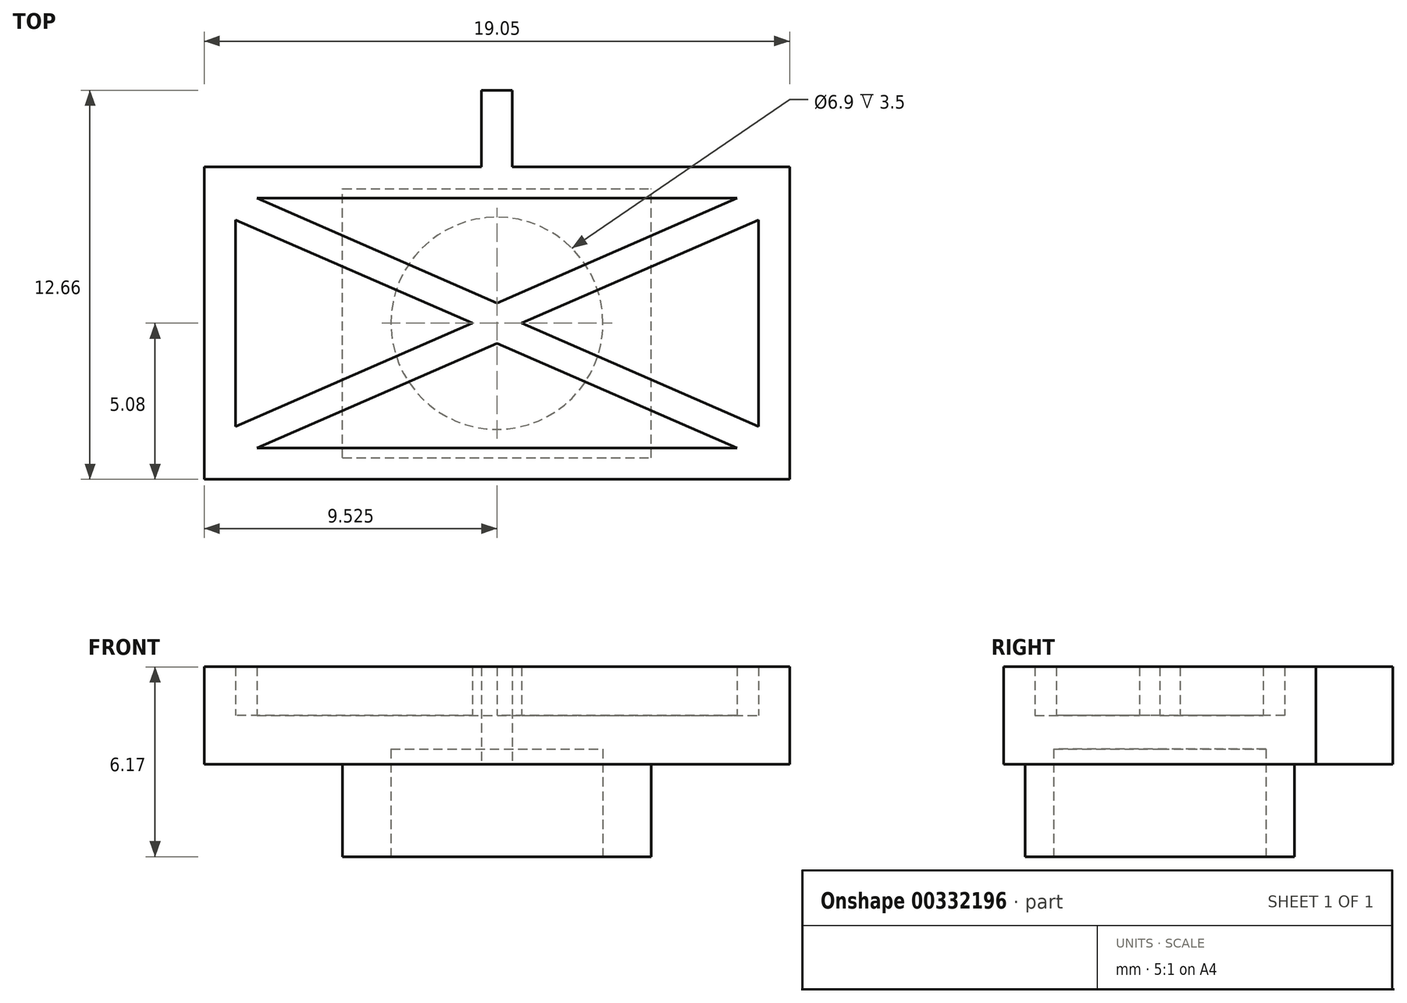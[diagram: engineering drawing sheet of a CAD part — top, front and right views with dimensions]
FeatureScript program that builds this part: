
annotation { "Feature Type Name" : "Feature", "Feature Type Description" : "" }
export const myFeature = defineFeature(function(context is Context, id is Id, definition is map)
    precondition{}
    {
        {
            var Q0;
            Q0=qCreatedBy(makeId("Top.planeOp"),FACE);
            var sketch = newSketch(context, id + "F0", { "sketchPlane" : qUnion([Q0])});
            skLineSegment(sketch, "E0.bottom", {"start": v(-19.05, 10.16) * mm, "end": v(0, 10.16) * mm});
            skLineSegment(sketch, "E0.top", {"start": v(-19.05, 0) * mm, "end": v(0, 0) * mm});
            skLineSegment(sketch, "E0.left", {"start": v(-19.05, 10.16) * mm, "end": v(-19.05, 0) * mm});
            skLineSegment(sketch, "E0.right", {"start": v(0, 10.16) * mm, "end": v(0, 0) * mm});
            skLineSegment(sketch, "E1", {"start": v(-9.52, 10.16) * mm, "end": v(-9.52, 0) * mm, "construction": true});
            skLineSegment(sketch, "E2.bottom", {"start": v(-10.02, 12.66) * mm, "end": v(-9.02, 12.66) * mm});
            skLineSegment(sketch, "E2.top", {"start": v(-10.02, 10.16) * mm, "end": v(-9.02, 10.16) * mm});
            skLineSegment(sketch, "E2.left", {"start": v(-10.02, 12.66) * mm, "end": v(-10.02, 10.16) * mm});
            skLineSegment(sketch, "E2.right", {"start": v(-9.02, 12.66) * mm, "end": v(-9.02, 10.16) * mm});
            skSolve(sketch);
        }
        {
            var Q0;
            Q0=qSketchRegion(id+"F0",true);
            extrude(context, id + "F1", {"entities" : qUnion([Q0]), "depth" : 3.17 * mm});
        }
        {
            var Q0;
            Q0=makeQuery(id+"F1.opExtrude","CAP_FACE",FACE,{"disambiguationData":[OSD([sQuery(id+"F0.wireOp",EDGE,"E0.bottom"),sQuery(id+"F0.wireOp",EDGE,"E0.top"),sQuery(id+"F0.wireOp",EDGE,"E0.left"),sQuery(id+"F0.wireOp",EDGE,"E0.right")])],"isStart":false});
            var sketch = newSketch(context, id + "F2", { "sketchPlane" : qUnion([Q0])});
            skLineSegment(sketch, "E3.bottom", {"start": v(-18.03, 9.14) * mm, "end": v(-1.02, 9.14) * mm});
            skLineSegment(sketch, "E3.top", {"start": v(-18.03, 1.02) * mm, "end": v(-1.02, 1.02) * mm});
            skLineSegment(sketch, "E3.left", {"start": v(-18.03, 9.14) * mm, "end": v(-18.03, 1.02) * mm});
            skLineSegment(sketch, "E3.right", {"start": v(-1.02, 9.14) * mm, "end": v(-1.02, 1.02) * mm});
            skSolve(sketch);
        }
        {
            var Q0;
            Q0=qSketchRegion(id+"F2",true);
            extrude(context, id + "F3", {"entities" : qUnion([Q0]), "operationType" : NewBodyOperationType.REMOVE, "oppositeDirection" : true, "depth" : 1.59 * mm});
        }
        {
            var Q0;
            {var subQ1=sQuery(id+"F2.wireOp",EDGE,"E3.top");var subQ4=makeQuery(id+"F3.boolean.opBoolean","COPY",FACE,{"derivedFrom":makeQuery(id+"F3.opExtrude","SWEPT_FACE",FACE,{"disambiguationData":[OSD([subQ1])]})});var subQ6=sQuery(id+"F2.wireOp",EDGE,"E3.right");Q0=makeQuery(id+"FbiU5rRMadnEj1Y_1.boolean.opBoolean","SPLIT",FACE,{"disambiguationData":[TD([subQ4])],"derivedFrom":makeQuery(id+"FD6hazfNaiJcgqe_1.boolean.opBoolean","SPLIT",FACE,{"disambiguationData":[TD([subQ4])],"derivedFrom":makeQuery(id+"F3.boolean.opBoolean","COPY",FACE,{"derivedFrom":makeQuery(id+"F3.opExtrude","CAP_FACE",FACE,{"disambiguationData":[OSD([sQuery(id+"F2.wireOp",EDGE,"E3.bottom"),subQ1,sQuery(id+"F2.wireOp",EDGE,"E3.left"),subQ6])],"isStart":false})})})});}
            var sketch = newSketch(context, id + "F4", { "sketchPlane" : qUnion([Q0])});
            skLineSegment(sketch, "E4", {"start": v(-19.05, 1.68) * mm, "end": v(-1.02, 1.68) * mm, "construction": true});
            skLineSegment(sketch, "E5", {"start": v(-9.53, 10.16) * mm, "end": v(-9.53, 0) * mm, "construction": true});
            skSolve(sketch);
        }
        {
            var Q0;
            Q0=makeQuery(id+"F1.opExtrude","CAP_FACE",FACE,{"disambiguationData":[OSD([sQuery(id+"F0.wireOp",EDGE,"E0.bottom"),sQuery(id+"F0.wireOp",EDGE,"E0.top"),sQuery(id+"F0.wireOp",EDGE,"E0.left"),sQuery(id+"F0.wireOp",EDGE,"E0.right"),sQuery(id+"F0.wireOp",EDGE,"iD4YVwzi-38ZZ-sZow-cuPB-LK5aPxXRs2tg"),sQuery(id+"F0.wireOp",EDGE,"25aa8db4-dd9b-41d2-b8c9-1594e9b75191"),sQuery(id+"F0.wireOp",EDGE,"40f63cb3-13d8-4821-a3c4-c05e674bd89b0.MirrorC")])],"isStart":true});
            var sketch = newSketch(context, id + "F5", { "sketchPlane" : qUnion([Q0])});
            skLineSegment(sketch, "E6.bottom", {"start": v(-14.55, -0.7) * mm, "end": v(-4.5, -0.7) * mm});
            skLineSegment(sketch, "E6.top", {"start": v(-14.55, -9.46) * mm, "end": v(-4.5, -9.46) * mm});
            skLineSegment(sketch, "E6.left", {"start": v(-14.55, -0.7) * mm, "end": v(-14.55, -9.46) * mm});
            skLineSegment(sketch, "E6.right", {"start": v(-4.5, -0.7) * mm, "end": v(-4.5, -9.46) * mm});
            skSolve(sketch);
        }
        {
            var Q0;
            Q0=qSketchRegion(id+"F5",true);
            extrude(context, id + "F6", {"entities" : qUnion([Q0]), "operationType" : NewBodyOperationType.ADD, "depth" : 3 * mm, "offsetDistance" : 25 * mm});
        }
        {
            var Q0;
            Q0=makeQuery(id+"F6.opExtrude","CAP_FACE",FACE,{"disambiguationData":[OSD([sQuery(id+"F5.wireOp",EDGE,"E6.bottom"),sQuery(id+"F5.wireOp",EDGE,"E6.top"),sQuery(id+"F5.wireOp",EDGE,"E6.left"),sQuery(id+"F5.wireOp",EDGE,"E6.right")])],"isStart":false});
            var sketch = newSketch(context, id + "F7", { "sketchPlane" : qUnion([Q0])});
            skCircle(sketch, "E7", {"center": v(-9.52, -5.08) * mm, "radius": 3.45 * mm});
            skLineSegment(sketch, "E8", {"start": v(-19.05, -5.08) * mm, "end": v(0, -5.08) * mm, "construction": true});
            skPoint(sketch, "E8.endSnap0", {"position": v(-4.5, -5.08) * mm});
            skLineSegment(sketch, "E9", {"start": v(-9.53, 0) * mm, "end": v(-9.53, -9.46) * mm, "construction": true});
            skSolve(sketch);
        }
        {
            var Q0;
            Q0=makeQuery(id+"F7.imprint","IMPRINT",FACE,{"disambiguationData":[TD([[makeQuery(id+"F7.imprint","IMPRINT",EDGE,{"derivedFrom":sQuery(id+"F7.wireOp",EDGE,"E7")}),1.0]])]});
            extrude(context, id + "F8", {"entities" : qUnion([Q0]), "operationType" : NewBodyOperationType.REMOVE, "oppositeDirection" : true, "depth" : 3.5 * mm, "offsetDistance" : 25 * mm});
        }
        {
            var Q0;
            Q0=makeQuery(id+"F4.imprint","IMPRINT",FACE,{"disambiguationData":[TD([[makeQuery(id+"F4.imprint","IMPRINT",EDGE,{"derivedFrom":makeQuery(id+"F3.boolean.opBoolean","COPY",EDGE,{"derivedFrom":makeQuery(id+"F3.opExtrude","CAP_EDGE",EDGE,{"disambiguationData":[OSD([sQuery(id+"F2.wireOp",EDGE,"E3.bottom")])],"isStart":false})})}),-1.0]])]});
            var sketch = newSketch(context, id + "F9", { "sketchPlane" : qUnion([Q0])});
            skLineSegment(sketch, "E10", {"start": v(-1.72, 9.14) * mm, "end": v(-9.53, 5.74) * mm});
            skLineSegment(sketch, "E11", {"start": v(-8.73, 5.08) * mm, "end": v(-1.02, 8.44) * mm});
            skLineSegment(sketch, "E12", {"start": v(-1.02, 8.44) * mm, "end": v(-1.02, 9.14) * mm});
            skLineSegment(sketch, "E13", {"start": v(-1.02, 9.14) * mm, "end": v(-1.72, 9.14) * mm});
            skLineSegment(sketch, "E14", {"start": v(-19.05, 5.08) * mm, "end": v(0, 5.08) * mm, "construction": true});
            skLineSegment(sketch, "E15.MirrorCS", {"start": v(-17.33, 9.14) * mm, "end": v(-9.53, 5.74) * mm});
            skLineSegment(sketch, "E16.MirrorCS", {"start": v(-10.33, 5.08) * mm, "end": v(-18.03, 8.44) * mm});
            skLineSegment(sketch, "E17.MirrorCS", {"start": v(-18.03, 8.44) * mm, "end": v(-18.03, 9.14) * mm});
            skLineSegment(sketch, "E18.MirrorCS", {"start": v(-18.03, 9.14) * mm, "end": v(-17.33, 9.14) * mm});
            skLineSegment(sketch, "E19.MirrorCS", {"start": v(-10.33, 5.08) * mm, "end": v(-18.03, 1.72) * mm});
            skLineSegment(sketch, "E20.MirrorCS", {"start": v(-8.73, 5.08) * mm, "end": v(-1.02, 1.72) * mm});
            skLineSegment(sketch, "E21.MirrorCS", {"start": v(-1.72, 1.02) * mm, "end": v(-9.53, 4.42) * mm});
            skLineSegment(sketch, "E22.MirrorCS", {"start": v(-17.33, 1.02) * mm, "end": v(-9.53, 4.42) * mm});
            skLineSegment(sketch, "E23.MirrorCS", {"start": v(-18.03, 1.02) * mm, "end": v(-17.33, 1.02) * mm});
            skLineSegment(sketch, "E24.MirrorCS", {"start": v(-18.03, 1.72) * mm, "end": v(-18.03, 1.02) * mm});
            skLineSegment(sketch, "E25.MirrorCS", {"start": v(-1.02, 1.72) * mm, "end": v(-1.02, 1.02) * mm});
            skLineSegment(sketch, "E26.MirrorCS", {"start": v(-1.02, 1.02) * mm, "end": v(-1.72, 1.02) * mm});
            skSolve(sketch);
        }
        {
            var Q0;
            Q0=qSketchRegion(id+"F9",true);
            var Q1;
            Q1=makeQuery(id+"FXsS83p9KQ4uv0L_1.boolean.opBoolean","MERGE",FACE,{"derivedFrom":[makeQuery(id+"F1.opExtrude","CAP_FACE",FACE,{"disambiguationData":[OSD([sQuery(id+"F0.wireOp",EDGE,"E0.bottom"),sQuery(id+"F0.wireOp",EDGE,"E0.top"),sQuery(id+"F0.wireOp",EDGE,"E0.left"),sQuery(id+"F0.wireOp",EDGE,"E0.right"),sQuery(id+"F0.wireOp",EDGE,"25aa8db4-dd9b-41d2-b8c9-1594e9b75191"),sQuery(id+"F0.wireOp",EDGE,"40f63cb3-13d8-4821-a3c4-c05e674bd89b0.MirrorC")])],"isStart":false}),makeQuery(id+"FbiU5rRMadnEj1Y_1.opExtrude","CAP_FACE",FACE,{"disambiguationData":[OSD([sQuery(id+"FmV1InaubWQgJeV_1.wireOp",EDGE,"lTleeF4S-0pnc-dI25-KJAR-2TLCTf0jWGc3"),sQuery(id+"FmV1InaubWQgJeV_1.wireOp",EDGE,"m9JDErra-axgF-Q1Zk-CJc0-x6RwavRCbCz8")])],"isStart":false}),makeQuery(id+"FXsS83p9KQ4uv0L_1.opExtrude","CAP_FACE",FACE,{"disambiguationData":[OSD([sQuery(id+"Fi3yzKCDt9pSW51_1.wireOp",EDGE,"cutzoVbR-JFbv-1kZ0-SQrw-pSLFGMZcN76v"),sQuery(id+"Fi3yzKCDt9pSW51_1.wireOp",EDGE,"XYQyWRLz-35l4-wHee-0FsY-Oat0KQk3jhR6"),sQuery(id+"Fi3yzKCDt9pSW51_1.wireOp",EDGE,"lBgadLLx-aQS8-kMAZ-d5qN-Zo8duSUxtBeX"),sQuery(id+"Fi3yzKCDt9pSW51_1.wireOp",EDGE,"DlRPRQGx-Alaq-SPUL-URFH-jddu6C2Nnp9z"),sQuery(id+"Fi3yzKCDt9pSW51_1.wireOp",EDGE,"Shc4e2eY-gIsf-lYKj-D0sO-212MCfLGw1w2"),sQuery(id+"Fi3yzKCDt9pSW51_1.wireOp",EDGE,"DXv1RSob-CDWK-uPmN-nh2c-bdjhB3yjVnB2"),sQuery(id+"Fi3yzKCDt9pSW51_1.wireOp",EDGE,"Mjf90MPI-7UZW-OfA1-fD3l-TGEU1IJ1uaYu"),sQuery(id+"Fi3yzKCDt9pSW51_1.wireOp",EDGE,"IrneLFi4-a4Xm-RgwH-oJvY-WcCPALNDAReP"),sQuery(id+"Fi3yzKCDt9pSW51_1.wireOp",EDGE,"toQdHavX-h7D1-dxbV-IXrh-P84p4AImceJh"),sQuery(id+"Fi3yzKCDt9pSW51_1.wireOp",EDGE,"xGw8HYbu-oKFY-4S3u-lNNy-w4TfAhwJFqQu"),sQuery(id+"Fi3yzKCDt9pSW51_1.wireOp",EDGE,"5pvZd2gl-M8UA-9HNZ-daD7-4TEjzgTyMgsA"),sQuery(id+"Fi3yzKCDt9pSW51_1.wireOp",EDGE,"b1702624-0c59-4015-bc2e-a5f6b81265a70.MirrorCS"),sQuery(id+"Fi3yzKCDt9pSW51_1.wireOp",EDGE,"7deeccc9-7886-4666-b44c-47b900ed28990.MirrorCS"),sQuery(id+"Fi3yzKCDt9pSW51_1.wireOp",EDGE,"75936777-967d-44d6-aacf-753113c8b50b0.MirrorCS"),sQuery(id+"Fi3yzKCDt9pSW51_1.wireOp",EDGE,"e5875930-5b2f-47d0-b261-f87a419dd3ea0.MirrorCS"),sQuery(id+"Fi3yzKCDt9pSW51_1.wireOp",EDGE,"e1f8200d-9078-41b5-85b4-8a4adb8dc9e80.MirrorCS"),sQuery(id+"Fi3yzKCDt9pSW51_1.wireOp",EDGE,"40fd4d9e-f758-4b42-b7b5-3e08d0cf58f50.MirrorCS"),sQuery(id+"Fi3yzKCDt9pSW51_1.wireOp",EDGE,"553d3a6c-e9a7-4b40-b1d3-0817f640e5cc0.MirrorCS"),sQuery(id+"Fi3yzKCDt9pSW51_1.wireOp",EDGE,"5a723a2c-c48e-43ea-a32e-a11b15ff1a7b0.MirrorCS"),sQuery(id+"Fi3yzKCDt9pSW51_1.wireOp",EDGE,"932d58c0-4b54-410d-a467-0e9cf49887c90.MirrorCS"),sQuery(id+"Fi3yzKCDt9pSW51_1.wireOp",EDGE,"eeedfdb4-aa26-4e83-bf33-b18388155c4d0.MirrorCS"),sQuery(id+"Fi3yzKCDt9pSW51_1.wireOp",EDGE,"a4c71cba-da55-4cc9-80cf-8947727491d80.MirrorCS")])],"isStart":false})]});
            extrude(context, id + "F10", {"entities" : qUnion([Q0]), "operationType" : NewBodyOperationType.ADD, "endBound" : BoundingType.UP_TO_SURFACE, "depth" : 25 * mm, "endBoundEntityFace" : qUnion([Q1]), "offsetDistance" : 25 * mm});
        }
    });
